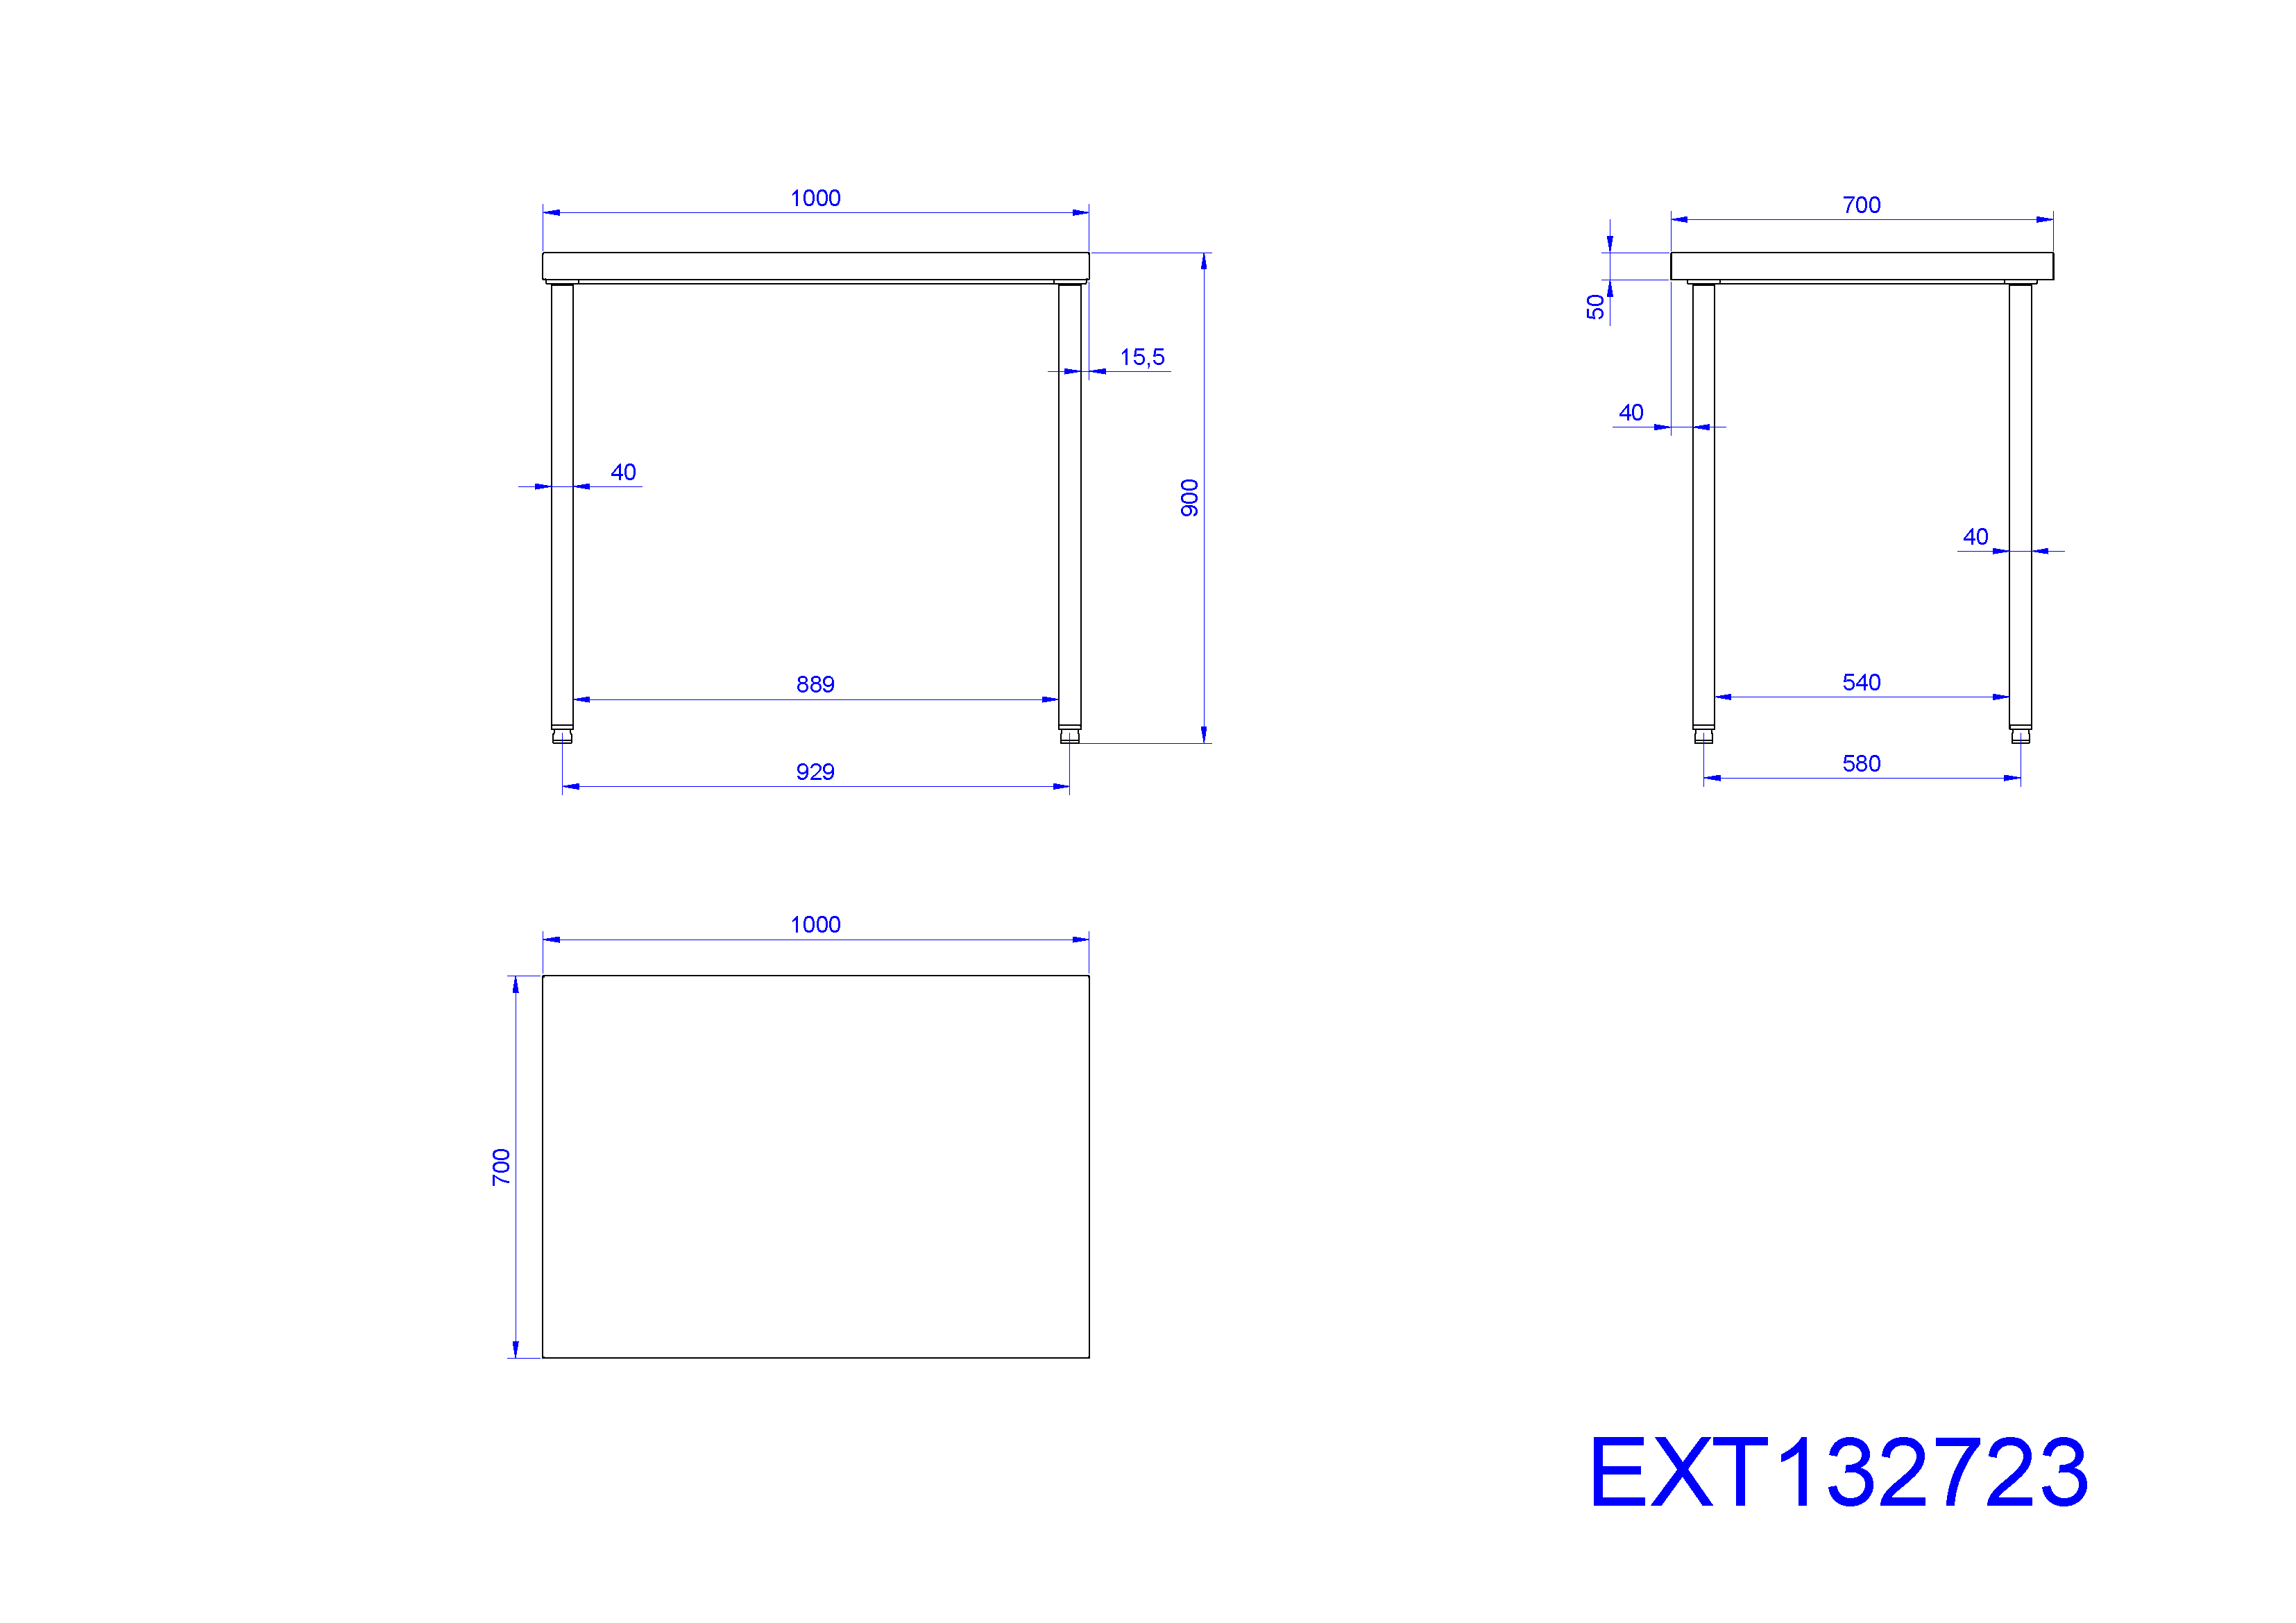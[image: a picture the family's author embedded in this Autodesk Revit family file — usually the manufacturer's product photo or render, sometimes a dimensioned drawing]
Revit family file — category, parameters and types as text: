
# Revit family: QF_ZANUSSI_132840_WTD1207N
name_source: partatom
category: Attrezzature speciali
units: mm (PartAtom-declared; Revit-internal decimal feet)

## family parameters
Basato su piano di lavoro = No
Condiviso = No
Punto di calcolo locali = No
Quota connettore circolare = Usa diametro
Sempre verticale = Sì
Taglio con vuoti quando caricato = No
Tipo di parte = Normale

## types (1)
- Standard
    Accessory = Sì
    Cold Water Size = 0 mm
    Compressed Air Pressure = 0.0 Pa
    Compressed Air Size = 0 mm
    Compressed Air Volume = 0.0 L/s
    Condensate Return Size = 0 mm
    Cycle = 0 Hz
    Depth Actual = 700 mm  [stored 2.29659 ft]
    Descrizione = WORK TABLE-DISASSEMBLED 1200MM
    Direct Waste Size = 0 mm
    Gas Input Pressure = 0
    Gas KW = 0
    Gas Size = 0 mm
    HP = 0 HP
    Height Actual = 900 mm  [stored 2.95276 ft]
    Hot Water Size = 0 mm
    Item Number = 132840
    Length Actual = 1200 mm
    Modello = WTD1207N
    Phase = 0
    Produttore = Zanussi
    Prospetto di default = 0 mm  [stored 0 ft]
    Refrigerant Compressor Remote = Sì
    Refrigeration Liquid Line Size = 0 mm  [stored 0 ft]
    Refrigeration Suction Line Size = 0 mm  [stored 0 ft]
    Steam Consumption per Hour = 0
    Steam Supply Maximum Pressure = 0.0 Pa
    Steam Supply Minimum Pressure = 0.0 Pa
    Steam Supply Size = 0 mm
    URL = http://www.zanussiprofessional.com
    URL Manufacturer = http://www.zanussiprofessional.com
    Volts = 0 V
    Watts = 0 W
    Weight = 43.00 kg

note: source unit labels omitted for Gas Input Pressure — the stored unit's dimension contradicts the parameter name (converter mislabeling)

note: [stored X ft] marks values corroborated as IEEE doubles in the binary element streams (Revit-internal decimal feet)

## geometry (parser evidence)
native form markers: Sweep x2
no freeform markers — native parametric forms only
